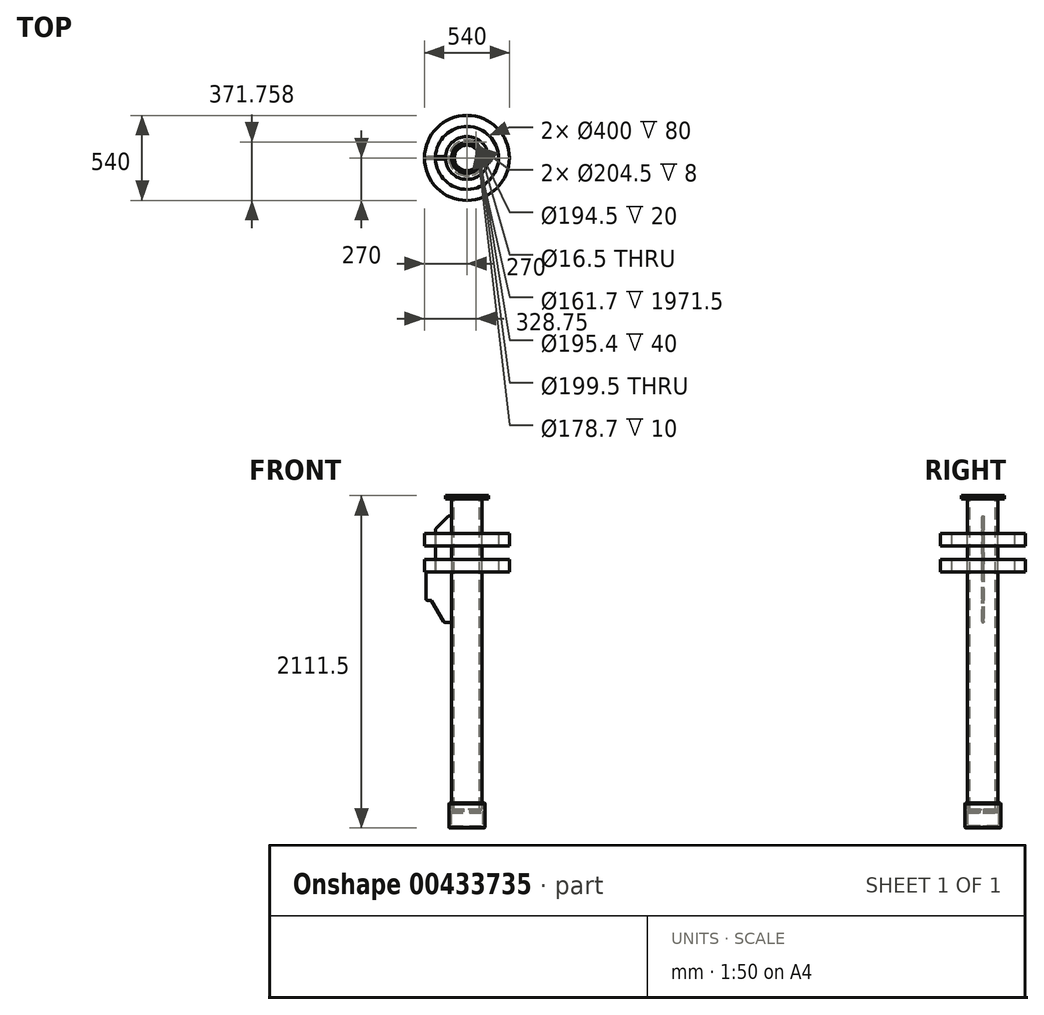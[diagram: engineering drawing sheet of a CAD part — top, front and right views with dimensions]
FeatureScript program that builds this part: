
annotation { "Feature Type Name" : "Feature", "Feature Type Description" : "" }
export const myFeature = defineFeature(function(context is Context, id is Id, definition is map)
    precondition{}
    {
        {
            var Q0;
            Q0=qCreatedBy(makeId("Top.planeOp"),FACE);
            var sketch = newSketch(context, id + "F0", { "sketchPlane" : qUnion([Q0])});
            skCircle(sketch, "E0", {"center": v(0, 0) * mm, "radius": 96.85 * mm});
            skCircle(sketch, "E1", {"center": v(0, 0) * mm, "radius": 80.85 * mm});
            skSolve(sketch);
        }
        {
            var Q0;
            Q0 = qSketchRegion(id + "F0", true);
            extrude(context, id + "F1", {"entities" : qUnion([Q0]), "oppositeDirection" : true, "depth" : 1971.5 * mm});
        }
        {
            var Q0;
            Q0=makeQuery(id+"F1.opExtrude","CAP_FACE",FACE,{"disambiguationData":[OSD([sQuery(id+"F0.wireOp",EDGE,"E0"),sQuery(id+"F0.wireOp",EDGE,"E1")])],"isStart":true});
            var sketch = newSketch(context, id + "F2", { "sketchPlane" : qUnion([Q0])});
            skCircle(sketch, "E2", {"center": v(0, 0) * mm, "radius": 136.5 * mm});
            skCircle(sketch, "E3", {"center": v(0, 0) * mm, "radius": 97.25 * mm});
            skSolve(sketch);
        }
        {
            var Q0;
            Q0 = qSketchRegion(id + "F2", true);
            extrude(context, id + "F3", {"entities" : qUnion([Q0]), "depth" : 20 * mm});
        }
        {
            var Q0;
            Q0=makeQuery(id+"F3.opExtrude","CAP_FACE",FACE,{"disambiguationData":[OSD([sQuery(id+"F2.wireOp",EDGE,"E2"),sQuery(id+"F2.wireOp",EDGE,"E3")])],"isStart":false});
            var sketch = newSketch(context, id + "F4", { "sketchPlane" : qUnion([Q0])});
            skCircle(sketch, "E4", {"center": v(0, 0) * mm, "radius": 117.5 * mm, "construction": true});
            skLineSegment(sketch, "E5", {"start": v(0, 0) * mm, "end": v(58.75, 101.76) * mm, "construction": true});
            skLineSegment(sketch, "E6", {"start": v(0, 0) * mm, "end": v(0, 117.5) * mm, "construction": true});
            skSolve(sketch);
        }
        {
            var Q0;
            Q0=sQuery(id+"F4.wireOp",VERTEX,"E5.end");
            var Q1;
            Q1=makeQuery(id+"F3.opExtrude","SWEPT_BODY",BODY,{"disambiguationData":[OSD([sQuery(id+"F2.wireOp",EDGE,"E2"),sQuery(id+"F2.wireOp",EDGE,"E3")])]});
            hole(context, id + "F5", {"style" : HoleStyle.SIMPLE, "endStyle" : HoleEndStyle.THROUGH, "holeDiameter" : 16.5 * mm, "isTappedThrough" : true, "tappedDepth" : 12.7 * mm, "tapClearance" : 3, "locations" : qUnion([Q0]), "scope" : qUnion([Q1])});
        }
        {
            var Q0;
            Q0=qCreatedBy(makeId("Front.planeOp"),FACE);
            var sketch = newSketch(context, id + "F6", { "sketchPlane" : qUnion([Q0])});
            skLineSegment(sketch, "E7.bottom", {"start": v(-200, -220) * mm, "end": v(-270, -220) * mm});
            skLineSegment(sketch, "E7.top", {"start": v(-200, -300) * mm, "end": v(-270, -300) * mm});
            skLineSegment(sketch, "E7.left", {"start": v(-200, -220) * mm, "end": v(-200, -300) * mm});
            skLineSegment(sketch, "E7.right", {"start": v(-270, -220) * mm, "end": v(-270, -300) * mm});
            skLineSegment(sketch, "E8.bottom", {"start": v(-200, -385) * mm, "end": v(-270, -385) * mm});
            skLineSegment(sketch, "E8.top", {"start": v(-200, -465) * mm, "end": v(-270, -465) * mm});
            skLineSegment(sketch, "E8.left", {"start": v(-200, -385) * mm, "end": v(-200, -465) * mm});
            skLineSegment(sketch, "E8.right", {"start": v(-270, -385) * mm, "end": v(-270, -465) * mm});
            skLineSegment(sketch, "E9", {"start": v(0, 0) * mm, "end": v(0, 342.74) * mm, "construction": true});
            skSolve(sketch);
        }
        {
            var Q0;
            Q0=makeQuery(id+"F6.imprint","IMPRINT",FACE,{"disambiguationData":[TD([[makeQuery(id+"F6.imprint","IMPRINT",EDGE,{"derivedFrom":sQuery(id+"F6.wireOp",EDGE,"E7.bottom")}),1.0]])]});
            var Q1;
            Q1=makeQuery(id+"F6.imprint","IMPRINT",FACE,{"disambiguationData":[TD([[makeQuery(id+"F6.imprint","IMPRINT",EDGE,{"derivedFrom":sQuery(id+"F6.wireOp",EDGE,"E8.bottom")}),1.0]])]});
            var Q2;
            Q2=makeQuery(id+"F1.opExtrude","SWEPT_FACE",FACE,{"disambiguationData":[OSD([sQuery(id+"F0.wireOp",EDGE,"E0")])]});
            revolve(context, id + "F7", {"entities" : qUnion([Q0, Q1]), "axis" : qUnion([Q2]), "revolveType" : RevolveType.FULL});
        }
        {
            var Q0;
            Q0=qCreatedBy(makeId("Front.planeOp"),FACE);
            var sketch = newSketch(context, id + "F8", { "sketchPlane" : qUnion([Q0])});
            skLineSegment(sketch, "E10", {"start": v(-96.85, -109.81) * mm, "end": v(-96.85, -783.81) * mm});
            skLineSegment(sketch, "E11", {"start": v(-96.85, -783.81) * mm, "end": v(-141.08, -783.81) * mm});
            skLineSegment(sketch, "E12", {"start": v(-260.85, -635.25) * mm, "end": v(-260.85, -465) * mm});
            skLineSegment(sketch, "E13", {"start": v(-260.85, -465) * mm, "end": v(-200, -465) * mm});
            skLineSegment(sketch, "E14", {"start": v(-200, -465) * mm, "end": v(-200, -197.1) * mm});
            skLineSegment(sketch, "E15", {"start": v(-197.07, -190.04) * mm, "end": v(-119.78, -112.74) * mm});
            skLineSegment(sketch, "E16", {"start": v(-112.7, -109.81) * mm, "end": v(-96.85, -109.81) * mm});
            skLineSegment(sketch, "E17", {"start": v(0, 0) * mm, "end": v(0, -195.76) * mm, "construction": true});
            skLineSegment(sketch, "E18", {"start": v(-149.74, -778.81) * mm, "end": v(-223.96, -650.25) * mm});
            skLineSegment(sketch, "E19", {"start": v(-232.62, -645.25) * mm, "end": v(-250.85, -645.25) * mm});
            skPoint(sketch, "E20.visualSharp", {"position": v(-146.85, -783.81) * mm});
            skArc(sketch, "E20.filletArc", {"start": v(-149.74, -778.81) * mm, "mid": v(-146.08, -782.47) * mm, "end": v(-141.08, -783.81) * mm});
            skPoint(sketch, "E21.visualSharp", {"position": v(-260.85, -645.25) * mm});
            skArc(sketch, "E21.filletArc", {"start": v(-260.85, -635.25) * mm, "mid": v(-257.92, -642.32) * mm, "end": v(-250.85, -645.25) * mm});
            skPoint(sketch, "E22.visualSharp", {"position": v(-226.85, -645.25) * mm});
            skArc(sketch, "E22.filletArc", {"start": v(-223.96, -650.25) * mm, "mid": v(-227.62, -646.59) * mm, "end": v(-232.62, -645.25) * mm});
            skPoint(sketch, "E23.visualSharp", {"position": v(-200, -192.96) * mm});
            skArc(sketch, "E23.filletArc", {"start": v(-197.07, -190.04) * mm, "mid": v(-199.24, -193.28) * mm, "end": v(-200, -197.1) * mm});
            skPoint(sketch, "E24.visualSharp", {"position": v(-116.85, -109.81) * mm});
            skArc(sketch, "E24.filletArc", {"start": v(-112.7, -109.81) * mm, "mid": v(-116.53, -110.58) * mm, "end": v(-119.78, -112.74) * mm});
            skSolve(sketch);
        }
        {
            var Q0;
            Q0 = qSketchRegion(id + "F8", true);
            extrude(context, id + "F9", {"entities" : qUnion([Q0]), "endBound" : BoundingType.SYMMETRIC, "depth" : 15 * mm});
        }
        {
            var Q0;
            Q0=qCreatedBy(makeId("Front.planeOp"),FACE);
            var sketch = newSketch(context, id + "F10", { "sketchPlane" : qUnion([Q0])});
            skLineSegment(sketch, "E25", {"start": v(-97.7, -1931.5) * mm, "end": v(-97.7, -1971.5) * mm});
            skLineSegment(sketch, "E26", {"start": v(-97.7, -1971.5) * mm, "end": v(-89.35, -1971.5) * mm});
            skLineSegment(sketch, "E27", {"start": v(-89.35, -1971.5) * mm, "end": v(-89.35, -1981.5) * mm});
            skLineSegment(sketch, "E28", {"start": v(-89.35, -1981.5) * mm, "end": v(-102.25, -1981.5) * mm});
            skLineSegment(sketch, "E29", {"start": v(-102.25, -1981.5) * mm, "end": v(-102.25, -1989.5) * mm});
            skLineSegment(sketch, "E30", {"start": v(-102.25, -1989.5) * mm, "end": v(-99.75, -1993.83) * mm});
            skLineSegment(sketch, "E31", {"start": v(-99.75, -1993.83) * mm, "end": v(-99.75, -2079.17) * mm});
            skLineSegment(sketch, "E32", {"start": v(-99.75, -2079.17) * mm, "end": v(-102.25, -2083.5) * mm});
            skLineSegment(sketch, "E33", {"start": v(-102.25, -2083.5) * mm, "end": v(-102.25, -2091.5) * mm});
            skLineSegment(sketch, "E34", {"start": v(-102.25, -2091.5) * mm, "end": v(-115, -2091.5) * mm});
            skLineSegment(sketch, "E35", {"start": v(-115, -2091.5) * mm, "end": v(-115, -1931.5) * mm});
            skLineSegment(sketch, "E36", {"start": v(-115, -1931.5) * mm, "end": v(-97.7, -1931.5) * mm});
            skLineSegment(sketch, "E37", {"start": v(0, -1897.57) * mm, "end": v(0, -2141.92) * mm, "construction": true});
            skSolve(sketch);
        }
        {
            var Q0;
            Q0 = qSketchRegion(id + "F10", true);
            var Q1;
            Q1=makeQuery(id+"F1.opExtrude","SWEPT_FACE",FACE,{"disambiguationData":[OSD([sQuery(id+"F0.wireOp",EDGE,"E0")])]});
            revolve(context, id + "F11", {"operationType" : NewBodyOperationType.ADD, "entities" : qUnion([Q0]), "axis" : qUnion([Q1]), "revolveType" : RevolveType.FULL});
        }
        {
            var Q0;
            Q0=makeQuery(id+"F11.opRevolve","SWEPT_EDGE",EDGE,{"disambiguationData":[OSD([sQuery(id+"F10.wireOp",EDGE,"E35"),sQuery(id+"F10.wireOp",EDGE,"E36")])]});
            chamfer(context, id + "F12", {"entities" : qUnion([Q0]), "chamferType" : ChamferType.OFFSET_ANGLE, "width" : 5 * mm, "oppositeDirection" : false, "angle" : 30 * degree, "tangentPropagation" : true});
        }
        {
            var Q0;
            Q0=makeQuery(id+"F11.opRevolve","SWEPT_EDGE",EDGE,{"disambiguationData":[OSD([sQuery(id+"F10.wireOp",EDGE,"E34"),sQuery(id+"F10.wireOp",EDGE,"E35")])]});
            chamfer(context, id + "F13", {"entities" : qUnion([Q0]), "width" : 5 * mm, "tangentPropagation" : true});
        }
    });
